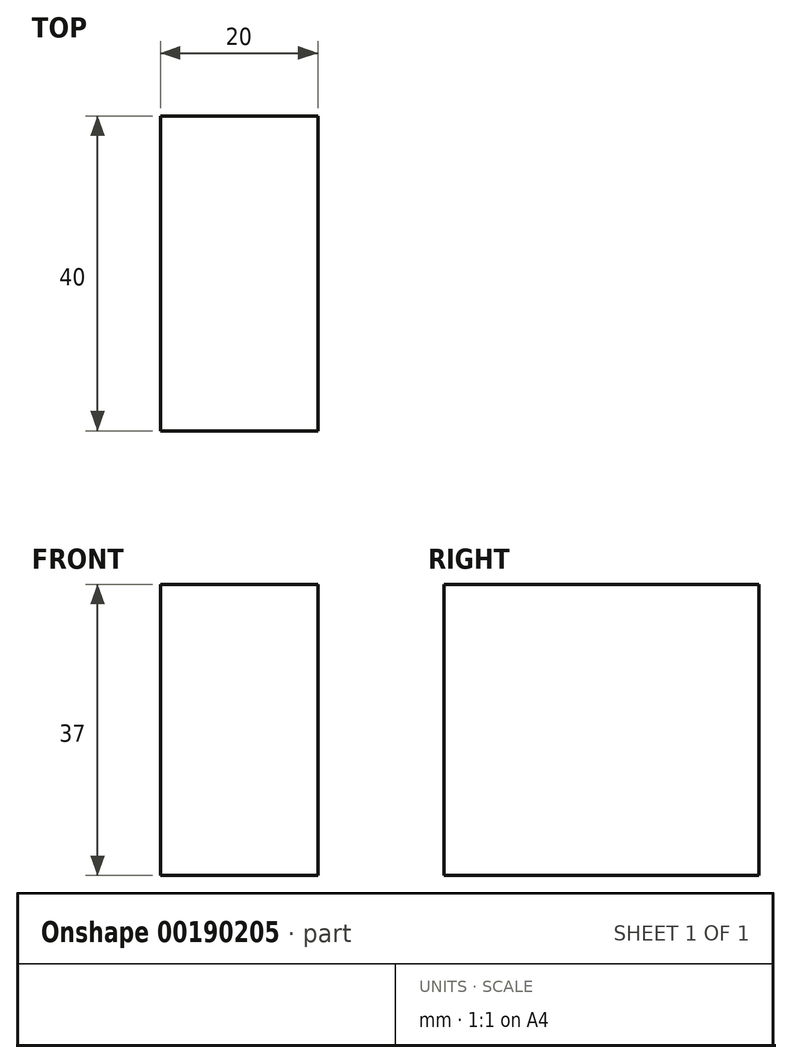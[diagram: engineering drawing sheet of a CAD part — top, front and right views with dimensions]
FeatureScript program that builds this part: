
annotation { "Feature Type Name" : "Feature", "Feature Type Description" : "" }
export const myFeature = defineFeature(function(context is Context, id is Id, definition is map)
    precondition{}
    {
        {
            var Q0;
            Q0=qCreatedBy(makeId("Top.planeOp"),FACE);
            var sketch = newSketch(context, id + "F0", { "sketchPlane" : qUnion([Q0])});
            skLineSegment(sketch, "E0.bottom", {"start": v(-17.5, 21.42) * mm, "end": v(2.5, 21.42) * mm});
            skLineSegment(sketch, "E0.top", {"start": v(-17.5, -18.58) * mm, "end": v(2.5, -18.58) * mm});
            skLineSegment(sketch, "E0.left", {"start": v(-17.5, 21.42) * mm, "end": v(-17.5, -18.58) * mm});
            skLineSegment(sketch, "E0.right", {"start": v(2.5, 21.42) * mm, "end": v(2.5, -18.58) * mm});
            skSolve(sketch);
        }
        {
            var Q0;
            Q0=makeQuery(id+"F0.imprint","IMPRINT",FACE,{"disambiguationData":[TD([[makeQuery(id+"F0.imprint","IMPRINT",EDGE,{"derivedFrom":sQuery(id+"F0.wireOp",EDGE,"E0.bottom")}),-1.0]])]});
            extrude(context, id + "F1", {"entities" : qUnion([Q0]), "depth" : 37 * mm, "offsetDistance" : 25 * mm});
        }
    });
